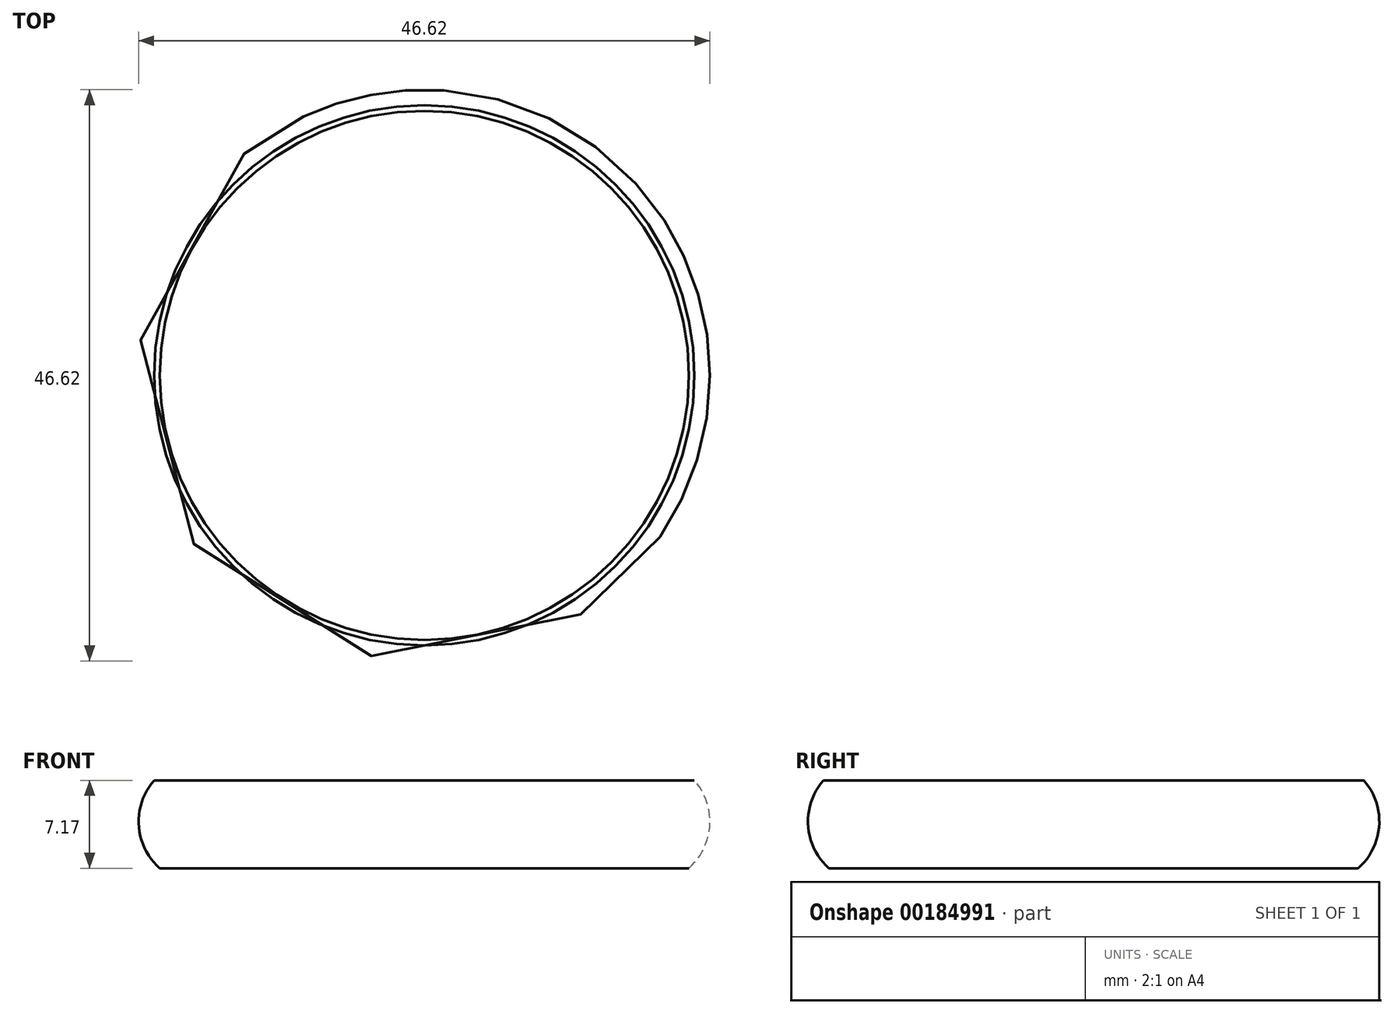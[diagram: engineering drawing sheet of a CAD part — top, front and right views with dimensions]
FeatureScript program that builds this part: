
annotation { "Feature Type Name" : "Feature", "Feature Type Description" : "" }
export const myFeature = defineFeature(function(context is Context, id is Id, definition is map)
    precondition{}
    {
        {
            var Q0;
            Q0=qCreatedBy(makeId("Top.planeOp"),FACE);
            var sketch = newSketch(context, id + "F0", { "sketchPlane" : qUnion([Q0])});
            skCircle(sketch, "E0", {"center": v(0, 0) * mm, "radius": 19.05 * mm});
            skCircle(sketch, "E1", {"center": v(0, 0) * mm, "radius": 21.59 * mm});
            skSolve(sketch);
        }
        {
            var Q0;
            Q0=qCreatedBy(makeId("Front.planeOp"),FACE);
            var sketch = newSketch(context, id + "F1", { "sketchPlane" : qUnion([Q0])});
            skLineSegment(sketch, "E2.0", {"start": v(-19.05, 0) * mm, "end": v(19.05, 0) * mm});
            skLineSegment(sketch, "E3.0", {"start": v(-21.59, 0) * mm, "end": v(21.59, 0) * mm});
            skLineSegment(sketch, "E4", {"start": v(-19.05, 0) * mm, "end": v(-19.05, 0) * mm});
            skLineSegment(sketch, "E5", {"start": v(21.59, 0) * mm, "end": v(21.59, 0) * mm});
            skLineSegment(sketch, "E6", {"start": v(22.04, 7.17) * mm, "end": v(22.04, 7.17) * mm});
            skPoint(sketch, "E7.visualSharp", {"position": v(25.4, 3.36) * mm});
            skArc(sketch, "E7.filletArc", {"start": v(21.59, 0) * mm, "mid": v(23.3, 3.5) * mm, "end": v(22.04, 7.17) * mm});
            skSolve(sketch);
        }
        {
            var Q0;
            Q0=sQuery(id+"F1.wireOp",EDGE,"E7.filletArc");
            var Q1;
            Q1=sQuery(id+"F0.wireOp",EDGE,"E1");
            revolve(context, id + "F2", {"bodyType" : ToolBodyType.SURFACE, "surfaceEntities" : qUnion([Q0]), "axis" : qUnion([Q1]), "revolveType" : RevolveType.FULL});
        }
    });
